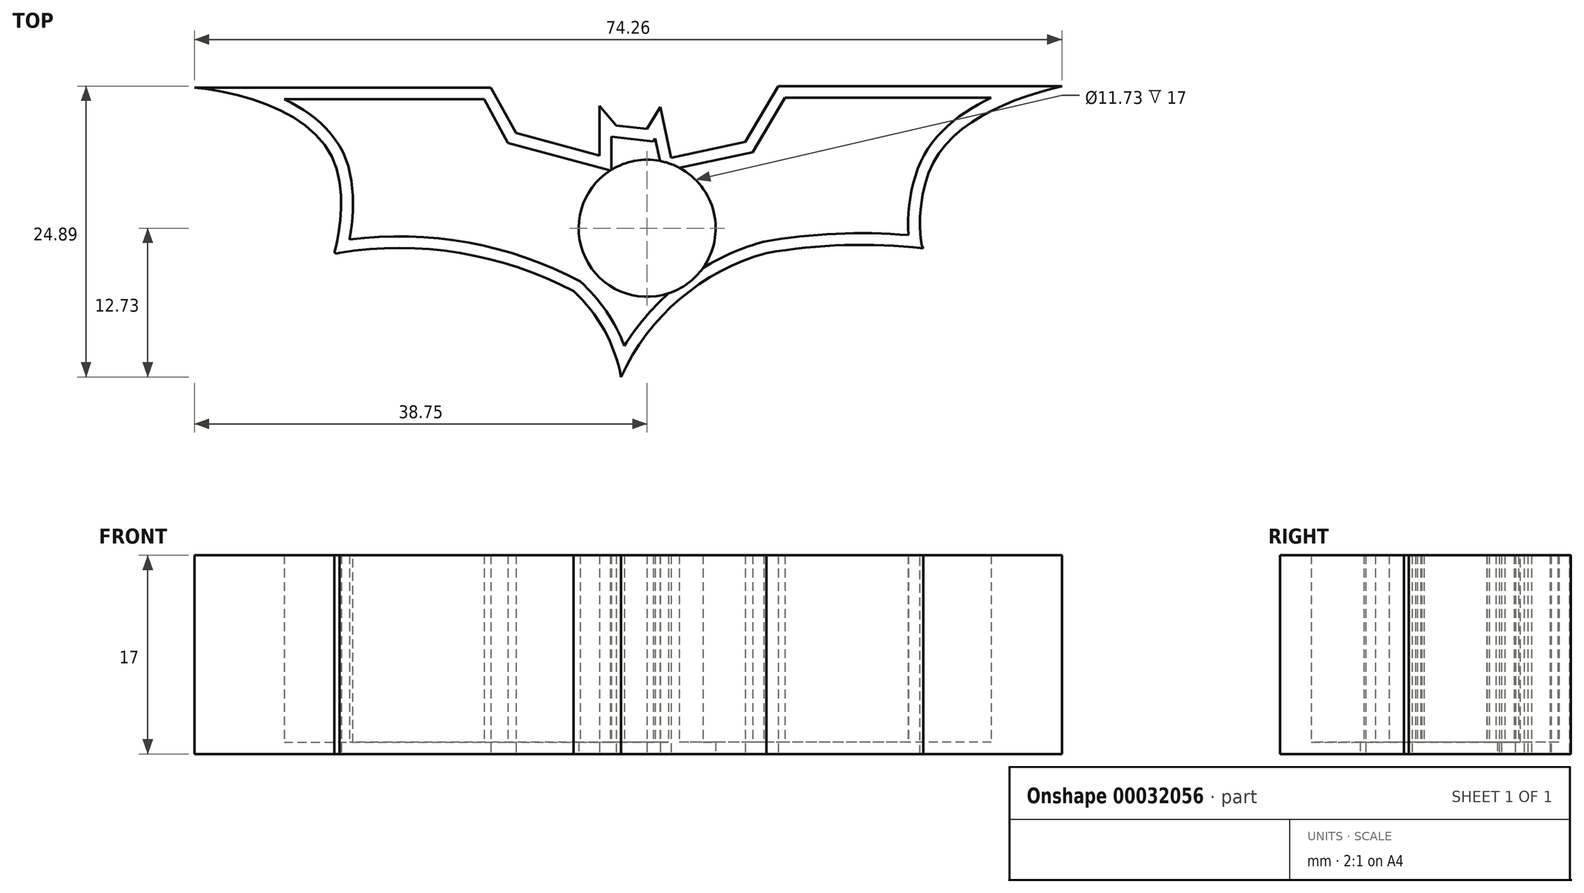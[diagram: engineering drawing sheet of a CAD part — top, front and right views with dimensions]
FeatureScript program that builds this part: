
annotation { "Feature Type Name" : "Feature", "Feature Type Description" : "" }
export const myFeature = defineFeature(function(context is Context, id is Id, definition is map)
    precondition{}
    {
        {
            var Q0;
            Q0=qCreatedBy(makeId("Top.planeOp"),FACE);
            var sketch = newSketch(context, id + "F0", { "sketchPlane" : qUnion([Q0])});
            skLineSegment(sketch, "E0", {"start": v(-38.75, 15.79) * mm, "end": v(-13.37, 15.79) * mm});
            skLineSegment(sketch, "E1", {"start": v(-13.37, 15.79) * mm, "end": v(-11.24, 11.91) * mm});
            skLineSegment(sketch, "E2", {"start": v(-11.24, 11.91) * mm, "end": v(-4.07, 9.98) * mm});
            skLineSegment(sketch, "E3", {"start": v(-4.07, 9.98) * mm, "end": v(-4.07, 14.24) * mm});
            skLineSegment(sketch, "E4", {"start": v(-4.07, 14.24) * mm, "end": v(-2.66, 12.55) * mm});
            skLineSegment(sketch, "E5", {"start": v(35.5, 15.91) * mm, "end": v(11.21, 15.91) * mm});
            skLineSegment(sketch, "E6", {"start": v(11.21, 15.91) * mm, "end": v(8.4, 11.14) * mm});
            skFitSpline(sketch, "E7", {"points": [v(-38.75, 15.79) * mm, v(-26.93, 9.78) * mm, v(-26.73, 1.84) * mm, v(-26.73, 1.65) * mm, v(-26.35, 1.65) * mm, v(-26.54, 2.23) * mm], "startDerivative": vector(29.24, -2.68) * mm, "endDerivative": vector(-4.67, 7.83) * mm});
            skFitSpline(sketch, "E8", {"points": [v(35.5, 15.91) * mm, v(24.4, 9.2) * mm, v(23.63, 2.03) * mm, v(23.83, 2.03) * mm], "startDerivative": vector(-24.43, -6.1) * mm, "endDerivative": vector(3.23, 1.56) * mm});
            skLineSegment(sketch, "E9", {"start": v(8.4, 11.14) * mm, "end": v(2.05, 9.8) * mm});
            skLineSegment(sketch, "E10", {"start": v(2.05, 9.8) * mm, "end": v(1.13, 14.12) * mm});
            skLineSegment(sketch, "E11", {"start": v(1.13, 14.12) * mm, "end": v(0, 12.24) * mm});
            skLineSegment(sketch, "E12", {"start": v(0, 12.24) * mm, "end": v(-2.66, 12.55) * mm});
            skArc(sketch, "E13", {"start": v(-6.32, -1.63) * mm, "mid": v(-16.06, 1.64) * mm, "end": v(-26.35, 1.65) * mm});
            skArc(sketch, "E14", {"start": v(-2.24, -8.98) * mm, "mid": v(-3.67, -4.97) * mm, "end": v(-6.32, -1.63) * mm});
            skArc(sketch, "E15", {"start": v(10.2, 1.63) * mm, "mid": v(2.81, -2.3) * mm, "end": v(-2.24, -8.98) * mm});
            skArc(sketch, "E16", {"start": v(23.63, 2.03) * mm, "mid": v(16.9, 2.3) * mm, "end": v(10.2, 1.63) * mm});
            skSolve(sketch);
        }
        {
            var Q0;
            {var subQ5=sQuery(id+"F0.wireOp",EDGE,"E0");Q0=makeQuery(id+"F0.imprint","IMPRINT",FACE,{"disambiguationData":[TD([[makeQuery(id+"F0.imprint","IMPRINT",EDGE,{"derivedFrom":subQ5}),-1.0]])]});}
            extrude(context, id + "F1", {"entities" : qUnion([Q0]), "depth" : 17 * mm});
        }
        {
            var Q0;
            Q0=makeQuery(id+"F1.opExtrude","CAP_FACE",FACE,{"disambiguationData":[OSD([sQuery(id+"F0.wireOp",EDGE,"E0"),sQuery(id+"F0.wireOp",EDGE,"E1"),sQuery(id+"F0.wireOp",EDGE,"E2"),sQuery(id+"F0.wireOp",EDGE,"E3"),sQuery(id+"F0.wireOp",EDGE,"E4"),sQuery(id+"F0.wireOp",EDGE,"E5"),sQuery(id+"F0.wireOp",EDGE,"E6"),sQuery(id+"F0.wireOp",EDGE,"E7"),sQuery(id+"F0.wireOp",EDGE,"E8"),sQuery(id+"F0.wireOp",EDGE,"E9"),sQuery(id+"F0.wireOp",EDGE,"E10"),sQuery(id+"F0.wireOp",EDGE,"E11"),sQuery(id+"F0.wireOp",EDGE,"E12"),sQuery(id+"F0.wireOp",EDGE,"E13"),sQuery(id+"F0.wireOp",EDGE,"E14"),sQuery(id+"F0.wireOp",EDGE,"E15"),sQuery(id+"F0.wireOp",EDGE,"E16")])],"isStart":false});
            shell(context, id + "F2", {"entities" : qUnion([Q0]), "thickness" : 1 * mm});
        }
        {
            var Q0;
            Q0=qCreatedBy(makeId("Top.planeOp"),FACE);
            var sketch = newSketch(context, id + "F3", { "sketchPlane" : qUnion([Q0])});
            skCircle(sketch, "E17", {"center": v(0, 3.75) * mm, "radius": 5.86 * mm});
            skSolve(sketch);
        }
        {
            var Q0;
            Q0=makeQuery(id+"F3.imprint","IMPRINT",FACE,{"disambiguationData":[TD([[makeQuery(id+"F3.imprint","IMPRINT",EDGE,{"derivedFrom":sQuery(id+"F3.wireOp",EDGE,"E17")}),1.0]])]});
            extrude(context, id + "F4", {"entities" : qUnion([Q0]), "operationType" : NewBodyOperationType.REMOVE, "depth" : 43.8 * mm});
        }
    });
